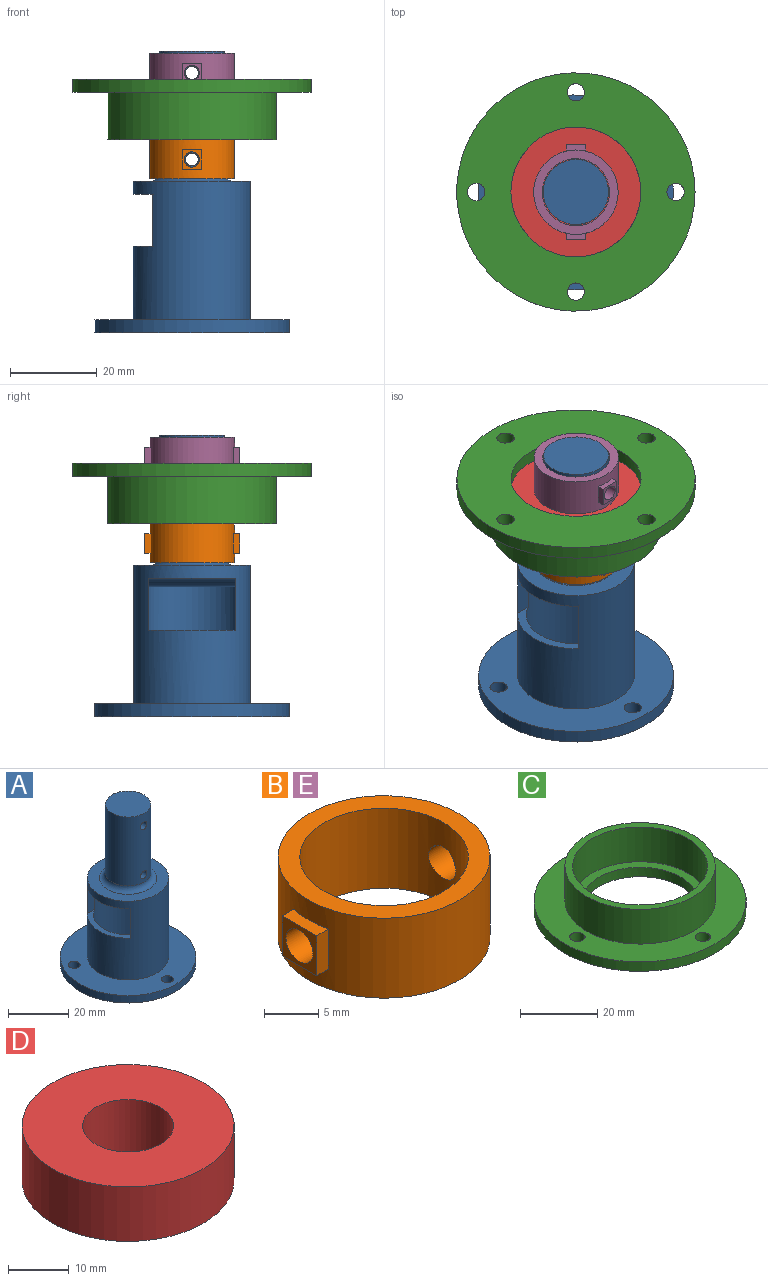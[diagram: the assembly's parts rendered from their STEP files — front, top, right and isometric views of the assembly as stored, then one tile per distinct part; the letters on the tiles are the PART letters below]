
ASSEMBLY  parts=5 mates=3
PART A: 20 faces, bbox 45x45x65 mm
  f0: cylinder r=7.5mm len=28mm, axis (0,0,-1), area 1290.9mm2, adj f11,f16,f18,f19
  f1: cylinder r=11.5mm len=30mm, axis (0,0,1), area 1925.2mm2, adj f3,f5,f12,f14,f15
  f2: cylinder r=13.5mm len=32mm, axis (0,0,-1), area 2444.1mm2, adj f6,f10,f12,f13,f14,f15
  f3: plane 23x17.18mm, normal (0,0,-1), area 139.3mm2, adj f1,f14,f15,f17
  f4: cylinder r=22.5mm len=45mm, axis (0,0,1), area 424.1mm2, adj f5,f6
  f5: plane 45x45mm, normal (0,0,-1), area 1137.3mm2, adj f1,f4,f7,f8,f9
  f6: plane 45x45mm, normal (0,0,1), area 980.2mm2, adj f2,f4,f7,f8,f9
  f7: cylinder r=2mm len=4mm, axis (0,0,1), area 37.7mm2, adj f5,f6
  f8: cylinder r=2mm len=4mm, axis (0,0,1), area 37.7mm2, adj f5,f6
  f9: cylinder r=2mm len=4mm, axis (0,0,1), area 37.7mm2, adj f5,f6
  f10: plane 27x27mm, normal (0,0,1), area 289mm2, adj f2,f16
  f11: plane 15x15mm, normal (0,0,1), area 176.7mm2, adj f0
  f12: plane 20x7.82mm, normal (0,0,1), area 46.5mm2, adj f1,f2,f14,f15
  f13: plane 20x13.5mm, normal (0,0,-1), area 242.7mm2, adj f2,f14,f15,f17
  f14: plane 13.07x12mm, normal (0,1,0), area 54.4mm2, adj f1,f2,f3,f12,f13,f17
  f15: plane 13.07x12mm, normal (0,-1,0), area 54.4mm2, adj f1,f2,f3,f12,f13,f17
  f16: torus R=9.5mm, axis (0,0,1), area 162.4mm2, adj f0,f10
  f17: cylinder r=5mm len=20mm, axis (0,1,0), area 92.7mm2, adj f3,f13,f14,f15
  f18: cylinder r=1.5mm len=15mm, axis (0,1,0), area 139.9mm2, adj f0
  f19: cylinder r=1.5mm len=15mm, axis (0,1,0), area 139.9mm2, adj f0
PART B: 16 faces, bbox 22x19.5x9 mm
  f0: cylinder r=9.75mm len=19.5mm, axis (0,0,1), area 510.5mm2, adj f2,f3,f4,f5,f6,f7,f9,f10
  f1: cylinder r=7.75mm len=15.5mm, axis (0,0,1), area 418.9mm2, adj f2,f3,f14,f15
  f2: plane 19.5x19.5mm, normal (0,0,-1), area 110mm2, adj f0,f1
  f3: plane 19.5x19.5mm, normal (0,0,1), area 110mm2, adj f0,f1
  f4: plane 4.5x1.51mm, normal (0,0,-1), area 6mm2, adj f0,f6,f7,f8
  f5: plane 4.5x1.51mm, normal (0,0,1), area 6mm2, adj f0,f6,f7,f8
  f6: plane 4.5x1.51mm, normal (0,-1,0), area 6.8mm2, adj f0,f4,f5,f8
  f7: plane 4.5x1.51mm, normal (0,1,0), area 6.8mm2, adj f0,f4,f5,f8
  f8: plane 4.5x4.5mm, normal (1,0,0), area 10.6mm2, adj f4,f5,f6,f7,f15
  f9: plane 4.5x1.51mm, normal (0,0,1), area 6mm2, adj f0,f11,f12,f13
  f10: plane 4.5x1.51mm, normal (0,0,-1), area 6mm2, adj f0,f11,f12,f13
  f11: plane 4.5x1.51mm, normal (0,-1,0), area 6.8mm2, adj f0,f9,f10,f13
  f12: plane 4.5x1.51mm, normal (0,1,0), area 6.8mm2, adj f0,f9,f10,f13
  f13: plane 4.5x4.5mm, normal (-1,0,0), area 10.6mm2, adj f9,f10,f11,f12,f14
  f14: cylinder r=1.75mm len=3.5mm, axis (1,0,0), area 36.8mm2, adj f1,f13
  f15: cylinder r=1.75mm len=3.5mm, axis (1,0,0), area 36.8mm2, adj f1,f8
PART C: 12 faces, bbox 55x55x14 mm
  f0: cylinder r=27.5mm len=55mm, axis (0,0,1), area 518.4mm2, adj f1,f2
  f1: plane 55x55mm, normal (0,0,-1), area 1618.7mm2, adj f0,f7,f8,f9,f10,f11
  f2: plane 55x55mm, normal (0,0,1), area 1131mm2, adj f0,f4,f7,f8,f9,f10
  f3: cylinder r=17.5mm len=35mm, axis (0,0,-1), area 1209.5mm2, adj f5,f6
  f4: cylinder r=19.5mm len=39mm, axis (0,0,-1), area 1347.7mm2, adj f2,f5
  f5: plane 39x39mm, normal (0,0,1), area 232.5mm2, adj f3,f4
  f6: plane 35x35mm, normal (0,0,1), area 255.3mm2, adj f3,f11
  f7: cylinder r=2mm len=4mm, axis (0,0,1), area 37.7mm2, adj f1,f2
  f8: cylinder r=2mm len=4mm, axis (0,0,1), area 37.7mm2, adj f1,f2
  f9: cylinder r=2mm len=4mm, axis (0,0,1), area 37.7mm2, adj f1,f2
  f10: cylinder r=2mm len=4mm, axis (0,0,1), area 37.7mm2, adj f1,f2
  f11: cylinder r=15mm len=30mm, axis (0,0,-1), area 282.7mm2, adj f1,f6
PART D: 4 faces, bbox 35x35x11 mm
  f0: cylinder r=7.5mm len=15mm, axis (0,0,-1), area 518.4mm2, adj f2,f3
  f1: cylinder r=17.5mm len=35mm, axis (0,0,-1), area 1209.5mm2, adj f2,f3
  f2: plane 35x35mm, normal (0,0,1), area 785.4mm2, adj f0,f1
  f3: plane 35x35mm, normal (0,0,-1), area 785.4mm2, adj f0,f1
PART E: same geometry as B
PLACE A t=(2.07,12.23,-9.45)mm
PLACE B rot(axis=(0.71,0.71,0),180deg) t=(2.07,12.16,23.05)mm
PLACE C rot(axis=(1,0,0),180deg) t=(2.07,12.23,43.05)mm
PLACE D t=(2.07,12.23,32.05)mm
PLACE E rot(axis=(0.71,0.71,0),180deg) t=(2.07,12.16,43.05)mm
MATE fastened C.f0 <-> D.f1  axis (0,0,-1) through (2.07,12.23,43.05)mm
MATE fastened D.f1 <-> A.f0  axis (0,0,1) through (2.07,12.23,43.05)mm
MATE fastened E.f14 <-> A.f18  axis (0,1,0) through (2.07,4.64,47.55)mm
